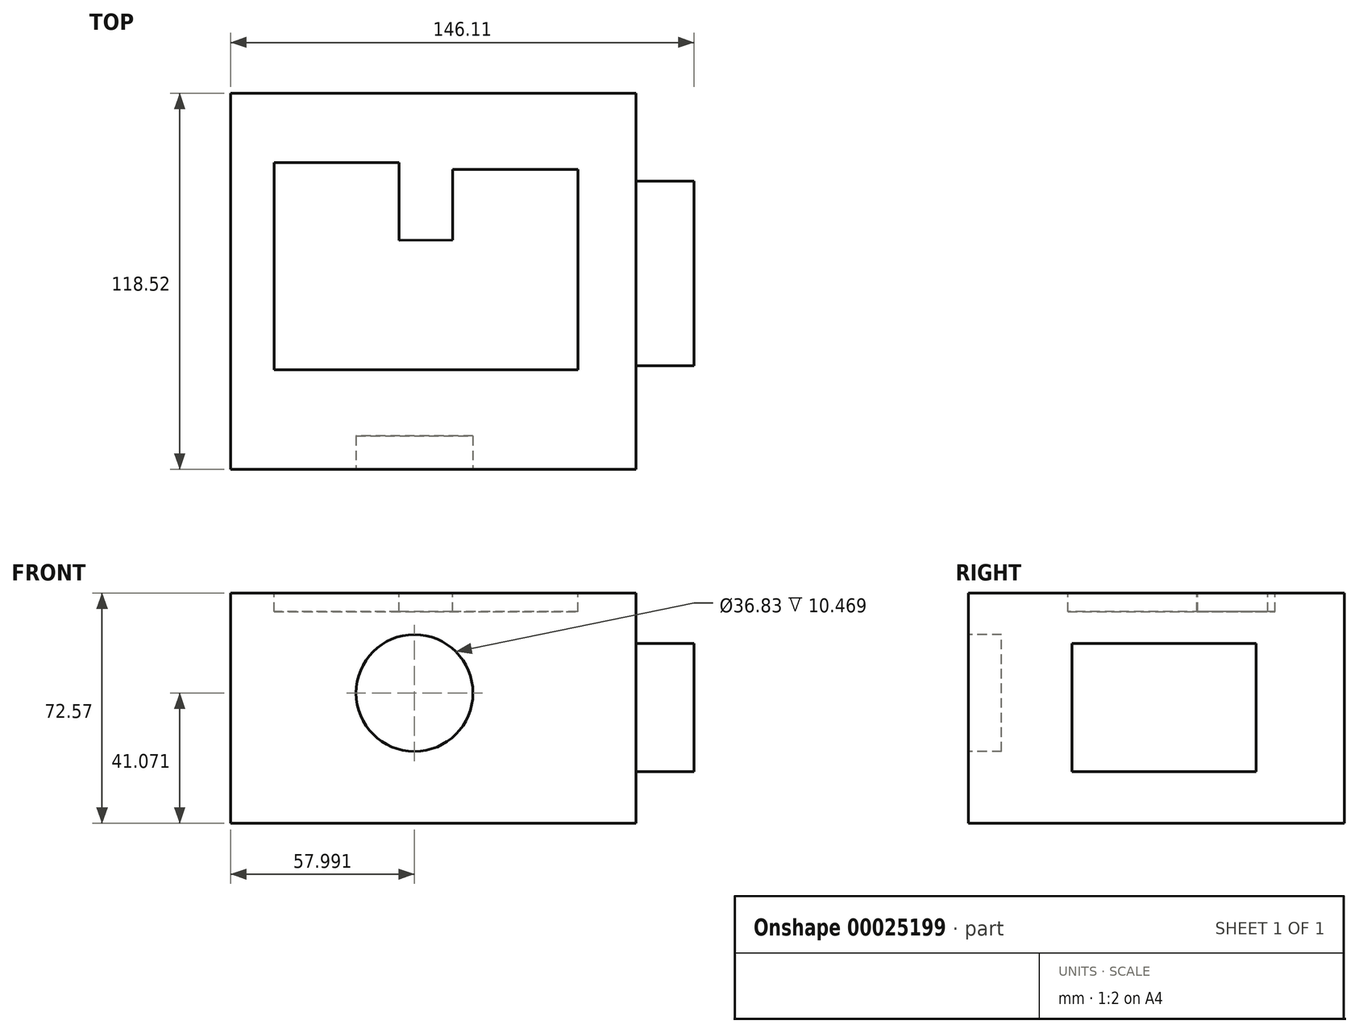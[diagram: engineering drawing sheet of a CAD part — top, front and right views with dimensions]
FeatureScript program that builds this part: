
annotation { "Feature Type Name" : "Feature", "Feature Type Description" : "" }
export const myFeature = defineFeature(function(context is Context, id is Id, definition is map)
    precondition{}
    {
        {
            var Q0;
            Q0=qCreatedBy(makeId("Top.planeOp"),FACE);
            var sketch = newSketch(context, id + "F0", { "sketchPlane" : qUnion([Q0])});
            skLineSegment(sketch, "E0.bottom", {"start": v(62.16, -56.2) * mm, "end": v(-65.7, -56.2) * mm});
            skLineSegment(sketch, "E0.top", {"start": v(62.16, 62.32) * mm, "end": v(-65.7, 62.32) * mm});
            skLineSegment(sketch, "E0.left", {"start": v(62.16, -56.2) * mm, "end": v(62.16, 62.32) * mm});
            skLineSegment(sketch, "E0.right", {"start": v(-65.7, -56.2) * mm, "end": v(-65.7, 62.32) * mm});
            skSolve(sketch);
        }
        {
            var Q0;
            Q0=makeQuery(id+"F0.imprint","IMPRINT",FACE,{"disambiguationData":[TD([[makeQuery(id+"F0.imprint","IMPRINT",EDGE,{"derivedFrom":sQuery(id+"F0.wireOp",EDGE,"E0.bottom")}),-1.0]])]});
            extrude(context, id + "F1", {"entities" : qUnion([Q0]), "depth" : 72.57 * mm});
        }
        {
            var Q0;
            Q0=makeQuery(id+"F1.opExtrude","SWEPT_FACE",FACE,{"disambiguationData":[OSD([sQuery(id+"F0.wireOp",EDGE,"E0.bottom")])]});
            var sketch = newSketch(context, id + "F2", { "sketchPlane" : qUnion([Q0])});
            skCircle(sketch, "E1", {"center": v(-7.7, 41.07) * mm, "radius": 18.42 * mm});
            skSolve(sketch);
        }
        {
            var Q0;
            Q0=makeQuery(id+"F2.imprint","IMPRINT",FACE,{"disambiguationData":[TD([[makeQuery(id+"F2.imprint","IMPRINT",EDGE,{"derivedFrom":sQuery(id+"F2.wireOp",EDGE,"E1")}),1.0]])]});
            extrude(context, id + "F3", {"entities" : qUnion([Q0]), "operationType" : NewBodyOperationType.REMOVE, "oppositeDirection" : true, "depth" : 10.47 * mm});
        }
        {
            var Q0;
            Q0=makeQuery(id+"F1.opExtrude","CAP_FACE",FACE,{"disambiguationData":[OSD([sQuery(id+"F0.wireOp",EDGE,"E0.bottom"),sQuery(id+"F0.wireOp",EDGE,"E0.top"),sQuery(id+"F0.wireOp",EDGE,"E0.left"),sQuery(id+"F0.wireOp",EDGE,"E0.right")])],"isStart":false});
            var sketch = newSketch(context, id + "F4", { "sketchPlane" : qUnion([Q0])});
            skLineSegment(sketch, "E2", {"start": v(-12.57, 15.88) * mm, "end": v(-12.57, 40.43) * mm});
            skLineSegment(sketch, "E3", {"start": v(-14.04, 40.43) * mm, "end": v(-51.92, 40.43) * mm});
            skLineSegment(sketch, "E4", {"start": v(-51.92, 40.43) * mm, "end": v(-51.92, -24.85) * mm});
            skLineSegment(sketch, "E5", {"start": v(-51.92, -24.85) * mm, "end": v(43.77, -24.85) * mm});
            skLineSegment(sketch, "E6", {"start": v(43.77, -24.85) * mm, "end": v(43.77, 38.25) * mm});
            skLineSegment(sketch, "E7", {"start": v(43.77, 38.25) * mm, "end": v(4.33, 38.25) * mm});
            skLineSegment(sketch, "E8", {"start": v(4.33, 38.25) * mm, "end": v(4.33, 16.06) * mm});
            skLineSegment(sketch, "E9", {"start": v(4.33, 16.06) * mm, "end": v(-12.57, 15.88) * mm});
            skLineSegment(sketch, "E10", {"start": v(-14.04, 40.43) * mm, "end": v(-12.57, 40.43) * mm});
            skSolve(sketch);
        }
        {
            var Q0;
            Q0=makeQuery(id+"F4.imprint","IMPRINT",FACE,{"disambiguationData":[TD([[makeQuery(id+"F4.imprint","IMPRINT",EDGE,{"derivedFrom":sQuery(id+"F4.wireOp",EDGE,"E2")}),1.0]])]});
            extrude(context, id + "F5", {"entities" : qUnion([Q0]), "operationType" : NewBodyOperationType.REMOVE, "oppositeDirection" : true, "depth" : 5.9 * mm});
        }
        {
            var Q0;
            Q0=makeQuery(id+"F1.opExtrude","SWEPT_FACE",FACE,{"disambiguationData":[OSD([sQuery(id+"F0.wireOp",EDGE,"E0.left")])]});
            var sketch = newSketch(context, id + "F6", { "sketchPlane" : qUnion([Q0])});
            skLineSegment(sketch, "E11.bottom", {"start": v(-23.52, 56.7) * mm, "end": v(34.55, 56.7) * mm});
            skLineSegment(sketch, "E11.top", {"start": v(-23.52, 16.32) * mm, "end": v(34.55, 16.32) * mm});
            skLineSegment(sketch, "E11.left", {"start": v(-23.52, 56.7) * mm, "end": v(-23.52, 16.32) * mm});
            skLineSegment(sketch, "E11.right", {"start": v(34.55, 56.7) * mm, "end": v(34.55, 16.32) * mm});
            skSolve(sketch);
        }
        {
            var Q0;
            Q0=makeQuery(id+"F6.imprint","IMPRINT",FACE,{"disambiguationData":[TD([[makeQuery(id+"F6.imprint","IMPRINT",EDGE,{"derivedFrom":sQuery(id+"F6.wireOp",EDGE,"E11.bottom")}),-1.0]])]});
            extrude(context, id + "F7", {"entities" : qUnion([Q0]), "operationType" : NewBodyOperationType.ADD, "depth" : 18.27 * mm});
        }
    });
